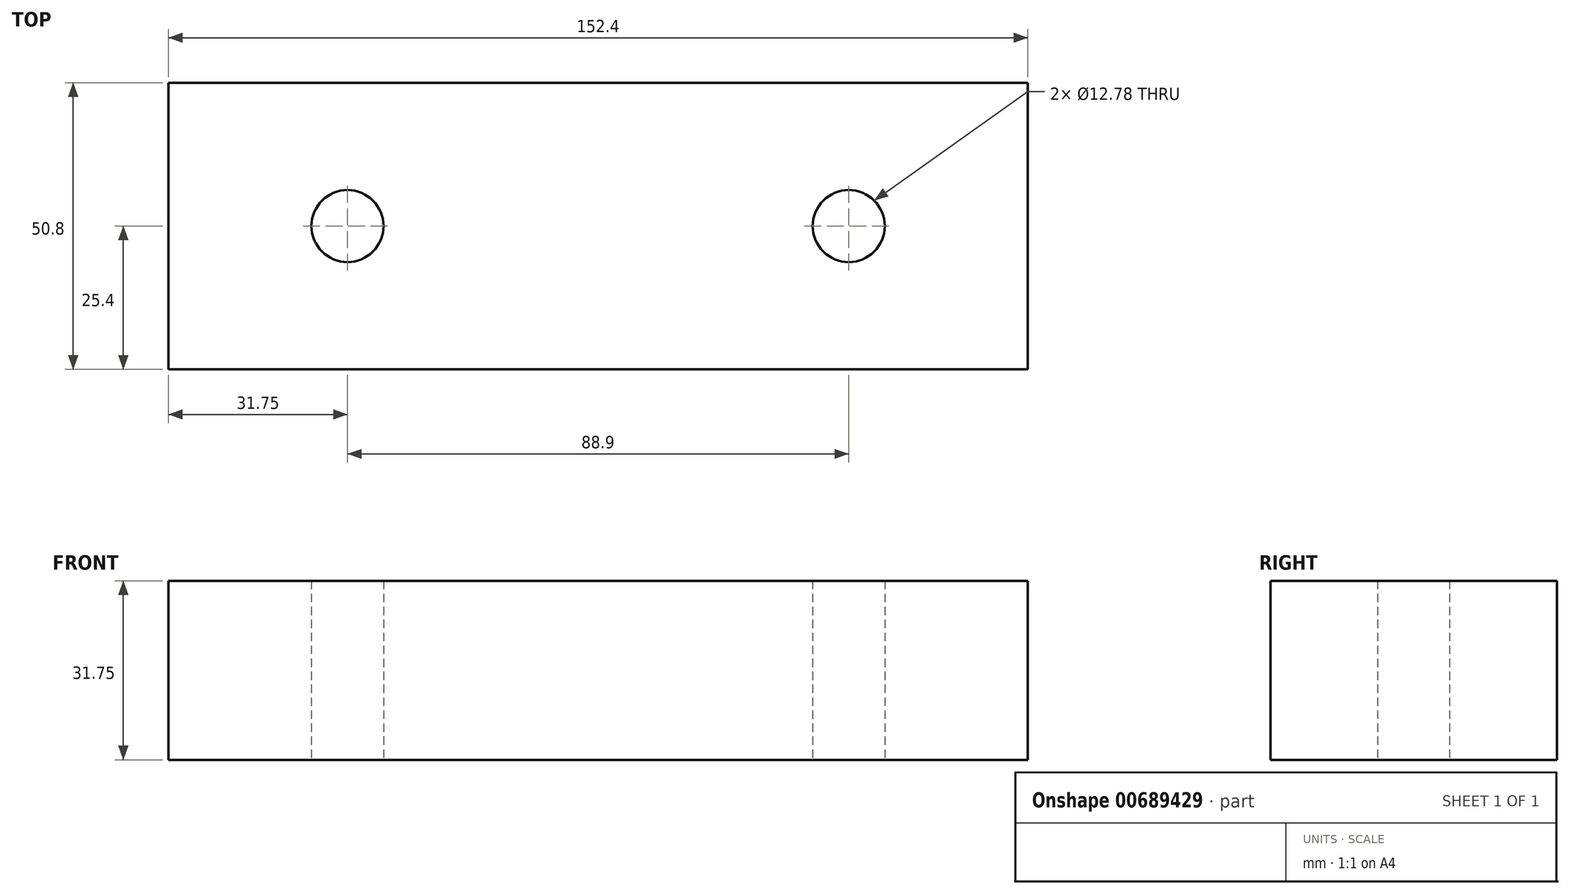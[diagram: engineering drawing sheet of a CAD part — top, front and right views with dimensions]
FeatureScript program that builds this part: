
annotation { "Feature Type Name" : "Feature", "Feature Type Description" : "" }
export const myFeature = defineFeature(function(context is Context, id is Id, definition is map)
    precondition{}
    {
        {
            var Q0;
            Q0=qCreatedBy(makeId("Top.planeOp"),FACE);
            var sketch = newSketch(context, id + "F0", { "sketchPlane" : qUnion([Q0])});
            skLineSegment(sketch, "E0.bottom", {"start": v(-76.2, 25.4) * mm, "end": v(76.2, 25.4) * mm});
            skLineSegment(sketch, "E0.top", {"start": v(-76.2, -25.4) * mm, "end": v(76.2, -25.4) * mm});
            skLineSegment(sketch, "E0.left", {"start": v(-76.2, 25.4) * mm, "end": v(-76.2, -25.4) * mm});
            skLineSegment(sketch, "E0.right", {"start": v(76.2, 25.4) * mm, "end": v(76.2, -25.4) * mm});
            skPoint(sketch, "E0.middle", {"position": v(0, 0) * mm});
            skCircle(sketch, "E1", {"center": v(-44.45, 0) * mm, "radius": 6.39 * mm});
            skCircle(sketch, "E2", {"center": v(44.45, 0) * mm, "radius": 6.39 * mm});
            skSolve(sketch);
        }
        {
            var Q0;
            Q0=makeQuery(id+"F0.imprint","IMPRINT",FACE,{"disambiguationData":[TD([[makeQuery(id+"F0.imprint","IMPRINT",EDGE,{"derivedFrom":sQuery(id+"F0.wireOp",EDGE,"E0.bottom")}),-1.0]])]});
            extrude(context, id + "F1", {"entities" : qUnion([Q0]), "depth" : 31.75 * mm, "offsetDistance" : 25.4 * mm});
        }
    });
